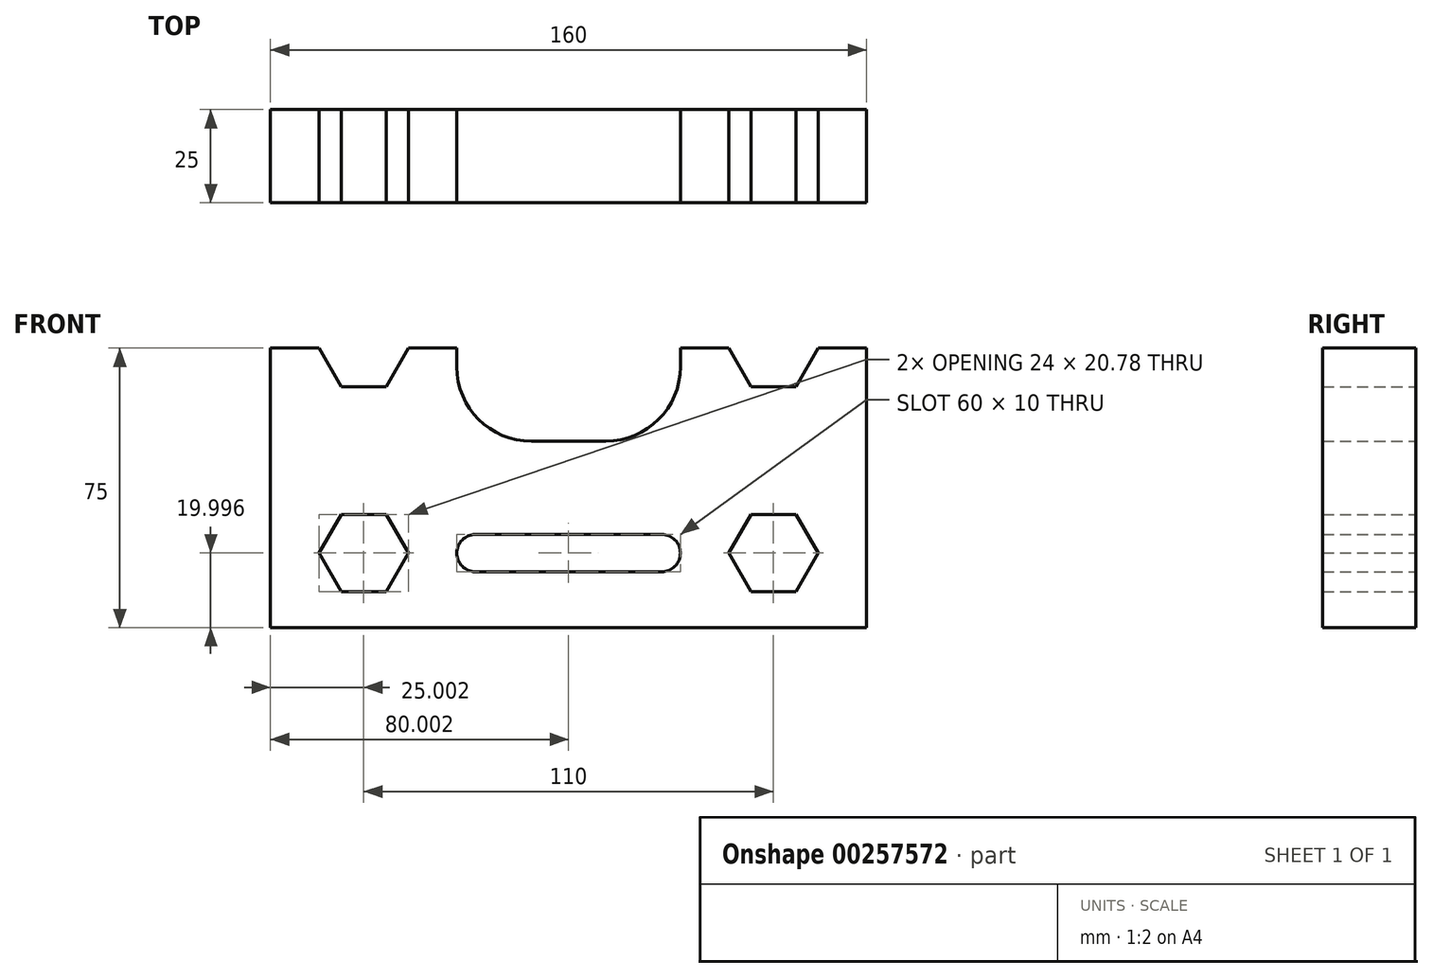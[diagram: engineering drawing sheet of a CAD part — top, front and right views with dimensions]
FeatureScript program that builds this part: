
annotation { "Feature Type Name" : "Feature", "Feature Type Description" : "" }
export const myFeature = defineFeature(function(context is Context, id is Id, definition is map)
    precondition{}
    {
        {
            var Q0;
            Q0=qCreatedBy(makeId("Front.planeOp"),FACE);
            var sketch = newSketch(context, id + "F0", { "sketchPlane" : qUnion([Q0])});
            skLineSegment(sketch, "E0.bottom", {"start": v(-107.76, 61.4) * mm, "end": v(-57.76, 61.4) * mm});
            skLineSegment(sketch, "E0.top", {"start": v(-107.76, -38.6) * mm, "end": v(52.24, -38.6) * mm});
            skLineSegment(sketch, "E0.left", {"start": v(-107.76, 61.4) * mm, "end": v(-107.76, -38.6) * mm});
            skLineSegment(sketch, "E0.right", {"start": v(52.24, 61.4) * mm, "end": v(52.24, -38.6) * mm});
            skLineSegment(sketch, "E1", {"start": v(-57.76, 61.4) * mm, "end": v(-57.76, 31.4) * mm});
            skLineSegment(sketch, "E2", {"start": v(-37.76, 11.4) * mm, "end": v(-17.76, 11.4) * mm});
            skLineSegment(sketch, "E3", {"start": v(2.24, 61.4) * mm, "end": v(2.24, 31.4) * mm});
            skLineSegment(sketch, "E4.trimOffspring", {"start": v(2.24, 61.4) * mm, "end": v(52.24, 61.4) * mm});
            skLineSegment(sketch, "E5", {"start": v(52.24, -38.6) * mm, "end": v(27.24, -38.6) * mm});
            skLineSegment(sketch, "E6", {"start": v(52.24, -38.6) * mm, "end": v(52.24, -18.6) * mm});
            skLineSegment(sketch, "E7", {"start": v(52.24, -18.6) * mm, "end": v(37.63, -18.6) * mm});
            skLineSegment(sketch, "E8", {"start": v(27.24, -38.6) * mm, "end": v(27.24, -28.99) * mm});
            skLineSegment(sketch, "E9", {"start": v(52.24, -38.6) * mm, "end": v(52.24, 36.4) * mm});
            skLineSegment(sketch, "E10", {"start": v(52.24, 36.4) * mm, "end": v(52.24, 36.4) * mm});
            skPoint(sketch, "E10.endSnap0", {"position": v(2.24, 36.4) * mm});
            skLineSegment(sketch, "E11", {"start": v(27.24, 0) * mm, "end": v(27.24, 52.03) * mm});
            skLineSegment(sketch, "E12", {"start": v(-107.76, -18.6) * mm, "end": v(-57.76, -18.6) * mm});
            skLineSegment(sketch, "E13", {"start": v(52.24, 36.4) * mm, "end": v(-72.37, 36.4) * mm});
            skLineSegment(sketch, "E14", {"start": v(-107.76, -38.6) * mm, "end": v(-82.76, -38.6) * mm});
            skLineSegment(sketch, "E15", {"start": v(-82.76, -38.6) * mm, "end": v(-82.76, -8.2) * mm});
            skCircle(sketch, "E16.cCircle", {"center": v(-82.76, 36.4) * mm, "radius": 10.4 * mm, "construction": true});
            skLineSegment(sketch, "E16.0", {"start": v(-70.76, 36.4) * mm, "end": v(-76.76, 26.01) * mm});
            skLineSegment(sketch, "E16.1", {"start": v(-76.76, 26.01) * mm, "end": v(-88.76, 26.01) * mm});
            skLineSegment(sketch, "E16.2", {"start": v(-88.76, 26.01) * mm, "end": v(-94.76, 36.4) * mm});
            skLineSegment(sketch, "E16.3", {"start": v(-94.76, 36.4) * mm, "end": v(-88.76, 46.8) * mm});
            skLineSegment(sketch, "E16.4", {"start": v(-88.76, 46.8) * mm, "end": v(-76.76, 46.8) * mm});
            skLineSegment(sketch, "E16.5", {"start": v(-76.76, 46.8) * mm, "end": v(-70.76, 36.4) * mm});
            skPoint(sketch, "E16.0.midPoint", {"position": v(-73.76, 31.2) * mm});
            skCircle(sketch, "E17.cCircle", {"center": v(27.24, 36.4) * mm, "radius": 10.4 * mm, "construction": true});
            skPoint(sketch, "E17.cCircle.centerSnap0", {"position": v(52.24, 36.4) * mm});
            skLineSegment(sketch, "E17.0", {"start": v(33.24, 26.01) * mm, "end": v(21.24, 26.01) * mm});
            skLineSegment(sketch, "E17.1", {"start": v(21.24, 26.01) * mm, "end": v(15.24, 36.4) * mm});
            skLineSegment(sketch, "E17.2", {"start": v(15.24, 36.4) * mm, "end": v(21.24, 46.8) * mm});
            skLineSegment(sketch, "E17.3", {"start": v(21.24, 46.8) * mm, "end": v(33.24, 46.8) * mm});
            skLineSegment(sketch, "E17.4", {"start": v(33.24, 46.8) * mm, "end": v(39.24, 36.4) * mm});
            skLineSegment(sketch, "E17.5", {"start": v(39.24, 36.4) * mm, "end": v(33.24, 26.01) * mm});
            skPoint(sketch, "E17.0.midPoint", {"position": v(27.24, 26.01) * mm});
            skCircle(sketch, "E18.cCircle", {"center": v(-82.76, -18.6) * mm, "radius": 10.4 * mm, "construction": true});
            skLineSegment(sketch, "E18.0", {"start": v(-70.76, -18.6) * mm, "end": v(-76.76, -28.99) * mm});
            skLineSegment(sketch, "E18.1", {"start": v(-76.76, -28.99) * mm, "end": v(-88.76, -28.99) * mm});
            skLineSegment(sketch, "E18.2", {"start": v(-88.76, -28.99) * mm, "end": v(-94.76, -18.6) * mm});
            skLineSegment(sketch, "E18.3", {"start": v(-94.76, -18.6) * mm, "end": v(-88.76, -8.2) * mm});
            skLineSegment(sketch, "E18.4", {"start": v(-88.76, -8.2) * mm, "end": v(-76.76, -8.2) * mm});
            skLineSegment(sketch, "E18.5", {"start": v(-76.76, -8.2) * mm, "end": v(-70.76, -18.6) * mm});
            skPoint(sketch, "E18.0.midPoint", {"position": v(-73.76, -23.8) * mm});
            skCircle(sketch, "E19.cCircle", {"center": v(27.24, -18.6) * mm, "radius": 10.4 * mm, "construction": true});
            skLineSegment(sketch, "E19.0", {"start": v(39.24, -18.6) * mm, "end": v(33.24, -28.99) * mm});
            skLineSegment(sketch, "E19.1", {"start": v(33.24, -28.99) * mm, "end": v(21.24, -28.99) * mm});
            skLineSegment(sketch, "E19.2", {"start": v(21.24, -28.99) * mm, "end": v(15.24, -18.6) * mm});
            skLineSegment(sketch, "E19.3", {"start": v(15.24, -18.6) * mm, "end": v(21.24, -8.2) * mm});
            skLineSegment(sketch, "E19.4", {"start": v(21.24, -8.2) * mm, "end": v(33.24, -8.2) * mm});
            skLineSegment(sketch, "E19.5", {"start": v(33.24, -8.2) * mm, "end": v(39.24, -18.6) * mm});
            skPoint(sketch, "E19.0.midPoint", {"position": v(36.24, -23.8) * mm});
            skPoint(sketch, "E20.visualSharp", {"position": v(2.24, 11.4) * mm});
            skArc(sketch, "E20.filletArc", {"start": v(-17.76, 11.4) * mm, "mid": v(-3.62, 17.26) * mm, "end": v(2.24, 31.4) * mm});
            skPoint(sketch, "E21.visualSharp", {"position": v(-57.76, 11.4) * mm});
            skArc(sketch, "E21.filletArc", {"start": v(-57.76, 31.4) * mm, "mid": v(-51.9, 17.26) * mm, "end": v(-37.76, 11.4) * mm});
            skLineSegment(sketch, "E22", {"start": v(-107.76, -38.6) * mm, "end": v(-52.76, -38.6) * mm});
            skLineSegment(sketch, "E23", {"start": v(-52.76, -23.6) * mm, "end": v(-52.76, -22.27) * mm});
            skLineSegment(sketch, "E24", {"start": v(-52.76, -38.6) * mm, "end": v(-2.76, -38.6) * mm});
            skCircle(sketch, "E25", {"center": v(-52.76, -18.6) * mm, "radius": 5 * mm});
            skPoint(sketch, "E25.centerSnap0", {"position": v(-52.76, -22.27) * mm});
            skLineSegment(sketch, "E26.trimOffspring", {"start": v(2.24, -18.6) * mm, "end": v(15.33, -18.6) * mm});
            skCircle(sketch, "E27", {"center": v(-2.76, -18.6) * mm, "radius": 5 * mm});
            skLineSegment(sketch, "E28", {"start": v(-52.76, -13.6) * mm, "end": v(0, -13.6) * mm});
            skLineSegment(sketch, "E29", {"start": v(-2.76, -23.6) * mm, "end": v(-52.76, -23.6) * mm});
            skPoint(sketch, "E30.trimOffspring.end.orphan", {"position": v(-82.76, 61.4) * mm});
            skLineSegment(sketch, "E31.trimOffspring", {"start": v(-82.76, 36.4) * mm, "end": v(-107.76, 36.4) * mm});
            skPoint(sketch, "E32.trimOffspring.end.orphan", {"position": v(-52.76, -5.95) * mm});
            skLineSegment(sketch, "E33.trimOffspring", {"start": v(27.24, -8.2) * mm, "end": v(27.24, 0) * mm});
            skLineSegment(sketch, "E34.trimOffspring", {"start": v(16.85, -18.6) * mm, "end": v(15.33, -18.6) * mm});
            skSolve(sketch);
        }
        {
            var Q0;
            Q0=makeQuery(id+"F0.imprint","IMPRINT",FACE,{"disambiguationData":[TD([[makeQuery(id+"F0.imprint","IMPRINT",EDGE,{"derivedFrom":sQuery(id+"F0.wireOp",EDGE,"E2")}),-1.0]])]});
            var Q1;
            {var subQ4=sQuery(id+"F0.wireOp",EDGE,"E0.bottom");Q1=makeQuery(id+"F0.imprint","IMPRINT",FACE,{"disambiguationData":[TD([[makeQuery(id+"F0.imprint","IMPRINT",EDGE,{"derivedFrom":subQ4}),-1.0]])]});}
            var Q2;
            {var subQ9=sQuery(id+"F0.wireOp",EDGE,"E18.2");Q2=makeQuery(id+"F0.imprint","IMPRINT",FACE,{"disambiguationData":[TD([[makeQuery(id+"F0.imprint","IMPRINT",EDGE,{"derivedFrom":subQ9}),1.0]])]});}
            var Q3;
            Q3=makeQuery(id+"F0.imprint","IMPRINT",FACE,{"disambiguationData":[TD([[makeQuery(id+"F0.imprint","IMPRINT",EDGE,{"derivedFrom":sQuery(id+"F0.wireOp",EDGE,"E0.top")}),1.0]])]});
            var Q4;
            {var subQ1=sQuery(id+"F0.wireOp",EDGE,"E5");Q4=makeQuery(id+"F0.imprint","IMPRINT",FACE,{"disambiguationData":[TD([[makeQuery(id+"F0.imprint","IMPRINT",EDGE,{"derivedFrom":subQ1}),-1.0]])]});}
            var Q5;
            {var subQ3=sQuery(id+"F0.wireOp",EDGE,"E17.5");Q5=makeQuery(id+"F0.imprint","IMPRINT",FACE,{"disambiguationData":[TD([[makeQuery(id+"F0.imprint","IMPRINT",EDGE,{"derivedFrom":subQ3}),1.0]])]});}
            var Q6;
            {var subQ1=sQuery(id+"F0.wireOp",EDGE,"E0.right");Q6=makeQuery(id+"F0.imprint","IMPRINT",FACE,{"disambiguationData":[TD([[makeQuery(id+"F0.imprint","IMPRINT",EDGE,{"derivedFrom":subQ1}),-1.0]])]});}
            extrude(context, id + "F1", {"entities" : qUnion([Q0, Q1, Q2, Q3, Q4, Q5, Q6]), "depth" : 25 * mm});
        }
    });
